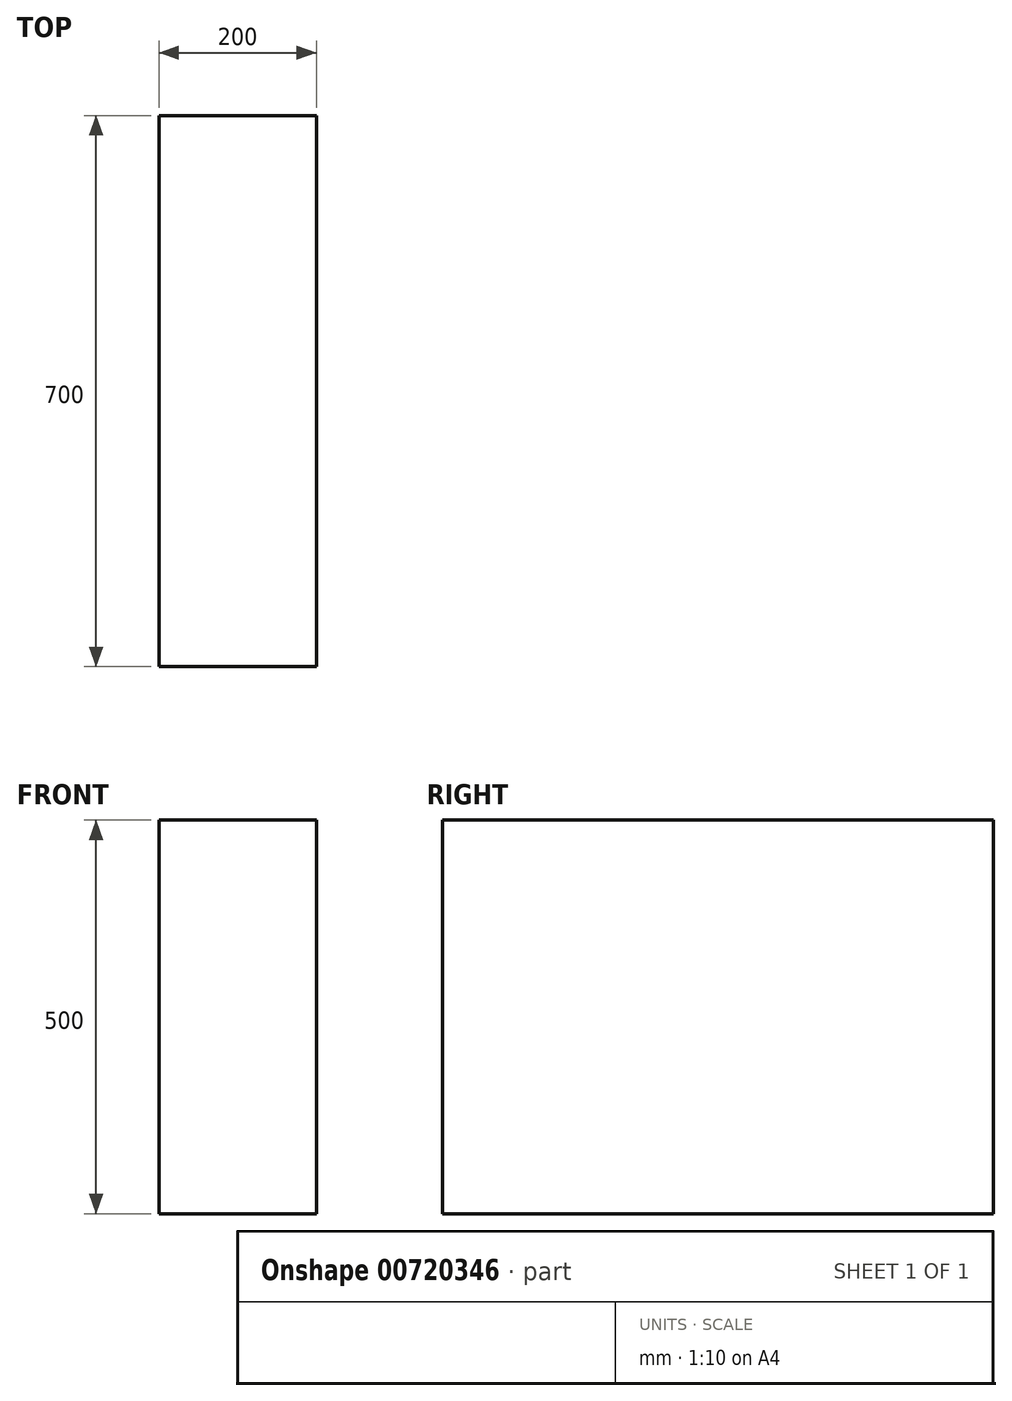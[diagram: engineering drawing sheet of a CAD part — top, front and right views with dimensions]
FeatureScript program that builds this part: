
annotation { "Feature Type Name" : "Feature", "Feature Type Description" : "" }
export const myFeature = defineFeature(function(context is Context, id is Id, definition is map)
    precondition{}
    {
        {
            var Q0;
            Q0=qCreatedBy(makeId("Front.planeOp"),FACE);
            var sketch = newSketch(context, id + "F0", { "sketchPlane" : qUnion([Q0])});
            skLineSegment(sketch, "E0.bottom", {"start": v(0, 0) * mm, "end": v(-200, 0) * mm});
            skLineSegment(sketch, "E0.top", {"start": v(0, -500) * mm, "end": v(-200, -500) * mm});
            skLineSegment(sketch, "E0.left", {"start": v(0, 0) * mm, "end": v(0, -500) * mm});
            skLineSegment(sketch, "E0.right", {"start": v(-200, 0) * mm, "end": v(-200, -500) * mm});
            skLineSegment(sketch, "E1.left", {"start": v(0, -500) * mm, "end": v(0, 0) * mm});
            skSolve(sketch);
        }
        {
            var Q0;
            Q0 = qSketchRegion(id + "F0", true);
            extrude(context, id + "F1", {"entities" : qUnion([Q0]), "depth" : 700 * mm, "offsetDistance" : 25 * mm});
        }
    });
